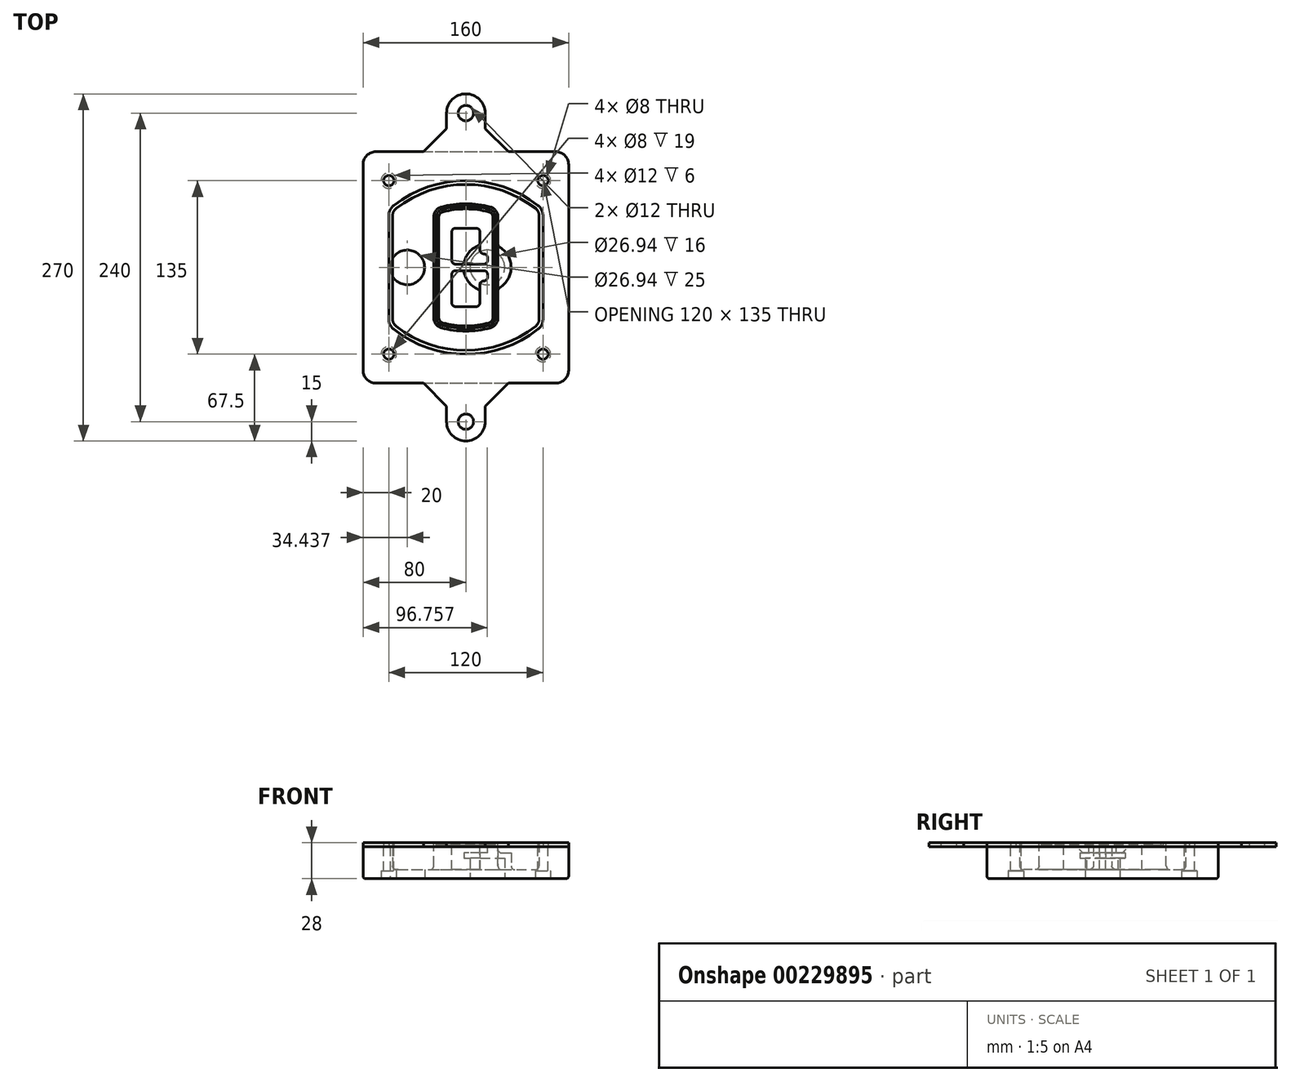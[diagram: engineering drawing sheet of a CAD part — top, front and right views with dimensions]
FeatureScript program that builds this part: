
annotation { "Feature Type Name" : "Feature", "Feature Type Description" : "" }
export const myFeature = defineFeature(function(context is Context, id is Id, definition is map)
    precondition{}
    {
        {
            var Q0;
            Q0=qCreatedBy(makeId("Top.planeOp"),FACE);
            var sketch = newSketch(context, id + "F0", { "sketchPlane" : qUnion([Q0])});
            skPoint(sketch, "E0.rect.middle", {"position": v(0, 0) * mm});
            skLineSegment(sketch, "E1.bottom", {"start": v(-70, -90) * mm, "end": v(70, -90) * mm});
            skLineSegment(sketch, "E1.top", {"start": v(-70, 90) * mm, "end": v(70, 90) * mm});
            skLineSegment(sketch, "E1.left", {"start": v(-80, -80) * mm, "end": v(-80, 80) * mm});
            skLineSegment(sketch, "E1.right", {"start": v(80, -80) * mm, "end": v(80, 80) * mm});
            skLineSegment(sketch, "E2", {"start": v(-80, 90) * mm, "end": v(80, -90) * mm, "construction": true});
            skLineSegment(sketch, "E3", {"start": v(80, 90) * mm, "end": v(-80, -90) * mm, "construction": true});
            skCircle(sketch, "E4", {"center": v(-60, 67.5) * mm, "radius": 4 * mm});
            skCircle(sketch, "E5", {"center": v(60, 67.5) * mm, "radius": 4 * mm});
            skCircle(sketch, "E6", {"center": v(60, -67.5) * mm, "radius": 4 * mm});
            skCircle(sketch, "E7", {"center": v(-60, -67.5) * mm, "radius": 4 * mm});
            skLineSegment(sketch, "E8", {"start": v(-60, 67.5) * mm, "end": v(60, 67.5) * mm, "construction": true});
            skLineSegment(sketch, "E9", {"start": v(60, 67.5) * mm, "end": v(60, -67.5) * mm, "construction": true});
            skLineSegment(sketch, "E10", {"start": v(60, -67.5) * mm, "end": v(-60, -67.5) * mm, "construction": true});
            skLineSegment(sketch, "E11", {"start": v(-60, -67.5) * mm, "end": v(-60, 67.5) * mm, "construction": true});
            skLineSegment(sketch, "E12", {"start": v(-60, 40.3) * mm, "end": v(-60, -40.3) * mm});
            skLineSegment(sketch, "E13", {"start": v(60, 40.3) * mm, "end": v(60, -40.3) * mm});
            skArc(sketch, "E14", {"start": v(56.15, 48.18) * mm, "mid": v(0, 67.5) * mm, "end": v(-56.15, 48.18) * mm});
            skArc(sketch, "E15", {"start": v(-56.15, -48.18) * mm, "mid": v(0, -67.5) * mm, "end": v(56.15, -48.18) * mm});
            skLineSegment(sketch, "E16", {"start": v(-60, 0) * mm, "end": v(60, 0) * mm, "construction": true});
            skPoint(sketch, "E17.visualSharp", {"position": v(-60, -45) * mm});
            skArc(sketch, "E17.filletArc", {"start": v(-60, -40.3) * mm, "mid": v(-58.99, -44.68) * mm, "end": v(-56.15, -48.18) * mm});
            skPoint(sketch, "E18.visualSharp", {"position": v(-60, 45) * mm});
            skArc(sketch, "E18.filletArc", {"start": v(-56.15, 48.18) * mm, "mid": v(-58.99, 44.68) * mm, "end": v(-60, 40.3) * mm});
            skPoint(sketch, "E19.visualSharp", {"position": v(60, 45) * mm});
            skArc(sketch, "E19.filletArc", {"start": v(60, 40.3) * mm, "mid": v(58.99, 44.68) * mm, "end": v(56.15, 48.18) * mm});
            skPoint(sketch, "E20.visualSharp", {"position": v(60, -45) * mm});
            skArc(sketch, "E20.filletArc", {"start": v(56.15, -48.18) * mm, "mid": v(58.99, -44.68) * mm, "end": v(60, -40.3) * mm});
            skPoint(sketch, "E21.visualSharp", {"position": v(-80, 90) * mm});
            skArc(sketch, "E21.filletArc", {"start": v(-70, 90) * mm, "mid": v(-77.07, 87.07) * mm, "end": v(-80, 80) * mm});
            skPoint(sketch, "E22.visualSharp", {"position": v(80, 90) * mm});
            skArc(sketch, "E22.filletArc", {"start": v(80, 80) * mm, "mid": v(77.07, 87.07) * mm, "end": v(70, 90) * mm});
            skPoint(sketch, "E23.visualSharp", {"position": v(80, -90) * mm});
            skArc(sketch, "E23.filletArc", {"start": v(70, -90) * mm, "mid": v(77.07, -87.07) * mm, "end": v(80, -80) * mm});
            skPoint(sketch, "E24.visualSharp", {"position": v(-80, -90) * mm});
            skArc(sketch, "E24.filletArc", {"start": v(-80, -80) * mm, "mid": v(-77.07, -87.07) * mm, "end": v(-70, -90) * mm});
            skArc(sketch, "E25.0", {"start": v(57, 40.3) * mm, "mid": v(56.3, 43.36) * mm, "end": v(54.3, 45.81) * mm});
            skLineSegment(sketch, "E25.1", {"start": v(57, 40.3) * mm, "end": v(57, -40.3) * mm});
            skArc(sketch, "E25.2", {"start": v(54.3, -45.81) * mm, "mid": v(56.3, -43.36) * mm, "end": v(57, -40.3) * mm});
            skArc(sketch, "E25.3", {"start": v(-54.3, -45.81) * mm, "mid": v(0, -64.5) * mm, "end": v(54.3, -45.81) * mm});
            skArc(sketch, "E25.4", {"start": v(-57, -40.3) * mm, "mid": v(-56.3, -43.36) * mm, "end": v(-54.3, -45.81) * mm});
            skArc(sketch, "E25.5", {"start": v(54.3, 45.81) * mm, "mid": v(0, 64.5) * mm, "end": v(-54.3, 45.81) * mm});
            skLineSegment(sketch, "E25.6", {"start": v(-57, 40.3) * mm, "end": v(-57, -40.3) * mm});
            skArc(sketch, "E25.7", {"start": v(-54.3, 45.81) * mm, "mid": v(-56.3, 43.36) * mm, "end": v(-57, 40.3) * mm});
            skArc(sketch, "E26.0", {"start": v(-58.62, 51.33) * mm, "mid": v(-62.58, 46.43) * mm, "end": v(-64, 40.3) * mm});
            skArc(sketch, "E26.1", {"start": v(58.62, 51.33) * mm, "mid": v(0, 71.5) * mm, "end": v(-58.62, 51.33) * mm});
            skArc(sketch, "E26.2", {"start": v(64, 40.3) * mm, "mid": v(62.58, 46.43) * mm, "end": v(58.62, 51.33) * mm});
            skLineSegment(sketch, "E26.3", {"start": v(64, 40.3) * mm, "end": v(64, -40.3) * mm});
            skArc(sketch, "E26.4", {"start": v(58.62, -51.33) * mm, "mid": v(62.58, -46.43) * mm, "end": v(64, -40.3) * mm});
            skLineSegment(sketch, "E26.5", {"start": v(-64, 40.3) * mm, "end": v(-64, -40.3) * mm});
            skArc(sketch, "E26.6", {"start": v(-58.62, -51.33) * mm, "mid": v(0, -71.5) * mm, "end": v(58.62, -51.33) * mm});
            skArc(sketch, "E26.7", {"start": v(-64, -40.3) * mm, "mid": v(-62.58, -46.43) * mm, "end": v(-58.62, -51.33) * mm});
            skSolve(sketch);
        }
        {
            var Q0;
            Q0=makeQuery(id+"F0.imprint","IMPRINT",FACE,{"disambiguationData":[TD([[makeQuery(id+"F0.imprint","IMPRINT",EDGE,{"derivedFrom":sQuery(id+"F0.wireOp",EDGE,"E1.bottom")}),1.0]])]});
            var Q1;
            Q1=makeQuery(id+"F0.imprint","IMPRINT",FACE,{"disambiguationData":[TD([[makeQuery(id+"F0.imprint","IMPRINT",EDGE,{"derivedFrom":sQuery(id+"F0.wireOp",EDGE,"E12")}),1.0]])]});
            var Q2;
            Q2=makeQuery(id+"F0.imprint","IMPRINT",FACE,{"disambiguationData":[TD([[makeQuery(id+"F0.imprint","IMPRINT",EDGE,{"derivedFrom":sQuery(id+"F0.wireOp",EDGE,"E25.0")}),1.0]])]});
            var Q3;
            Q3=makeQuery(id+"F0.imprint","IMPRINT",FACE,{"disambiguationData":[TD([[makeQuery(id+"F0.imprint","IMPRINT",EDGE,{"derivedFrom":sQuery(id+"F0.wireOp",EDGE,"E12")}),-1.0]])]});
            extrude(context, id + "F1", {"entities" : qUnion([Q0, Q1, Q2, Q3]), "oppositeDirection" : true, "depth" : 25 * mm});
        }
        {
            var Q0;
            Q0=makeQuery(id+"F0.imprint","IMPRINT",FACE,{"disambiguationData":[TD([[makeQuery(id+"F0.imprint","IMPRINT",EDGE,{"derivedFrom":sQuery(id+"F0.wireOp",EDGE,"E12")}),1.0]])]});
            extrude(context, id + "F2", {"entities" : qUnion([Q0]), "operationType" : NewBodyOperationType.ADD, "depth" : 3 * mm});
        }
        {
            var Q0;
            Q0=makeQuery(id+"F0.imprint","IMPRINT",FACE,{"disambiguationData":[TD([[makeQuery(id+"F0.imprint","IMPRINT",EDGE,{"derivedFrom":sQuery(id+"F0.wireOp",EDGE,"E25.0")}),1.0]])]});
            extrude(context, id + "F3", {"entities" : qUnion([Q0]), "operationType" : NewBodyOperationType.REMOVE, "oppositeDirection" : true, "depth" : 18 * mm});
        }
        {
            var Q0;
            Q0=makeQuery(id+"F2.opExtrude","CAP_FACE",FACE,{"disambiguationData":[OSD([sQuery(id+"F0.wireOp",EDGE,"E12"),sQuery(id+"F0.wireOp",EDGE,"E13"),sQuery(id+"F0.wireOp",EDGE,"E14"),sQuery(id+"F0.wireOp",EDGE,"E15"),sQuery(id+"F0.wireOp",EDGE,"E17.filletArc"),sQuery(id+"F0.wireOp",EDGE,"E18.filletArc"),sQuery(id+"F0.wireOp",EDGE,"E19.filletArc"),sQuery(id+"F0.wireOp",EDGE,"E20.filletArc"),sQuery(id+"F0.wireOp",EDGE,"E25.0"),sQuery(id+"F0.wireOp",EDGE,"E25.1"),sQuery(id+"F0.wireOp",EDGE,"E25.2"),sQuery(id+"F0.wireOp",EDGE,"E25.3"),sQuery(id+"F0.wireOp",EDGE,"E25.4"),sQuery(id+"F0.wireOp",EDGE,"E25.5"),sQuery(id+"F0.wireOp",EDGE,"E25.6"),sQuery(id+"F0.wireOp",EDGE,"E25.7")])],"isStart":false});
            var sketch = newSketch(context, id + "F4", { "sketchPlane" : qUnion([Q0])});
            skArc(sketch, "E27.0", {"start": v(-19.08, -46.97) * mm, "mid": v(0, -49.5) * mm, "end": v(19.08, -46.97) * mm});
            skArc(sketch, "E28.0", {"start": v(19.08, 46.97) * mm, "mid": v(0, 49.5) * mm, "end": v(-19.08, 46.97) * mm});
            skLineSegment(sketch, "E29", {"start": v(-25, 39.25) * mm, "end": v(-25, -39.25) * mm});
            skLineSegment(sketch, "E30", {"start": v(25, 39.25) * mm, "end": v(25, -39.25) * mm});
            skLineSegment(sketch, "E31", {"start": v(-25, 45.1) * mm, "end": v(25, 45.1) * mm, "construction": true});
            skLineSegment(sketch, "E32", {"start": v(-25, -45.1) * mm, "end": v(25, -45.1) * mm, "construction": true});
            skPoint(sketch, "E33.visualSharp", {"position": v(-25, 45.1) * mm});
            skArc(sketch, "E33.filletArc", {"start": v(-19.08, 46.97) * mm, "mid": v(-23.35, 44.11) * mm, "end": v(-25, 39.25) * mm});
            skPoint(sketch, "E34.visualSharp", {"position": v(25, 45.1) * mm});
            skArc(sketch, "E34.filletArc", {"start": v(25, 39.25) * mm, "mid": v(23.35, 44.11) * mm, "end": v(19.08, 46.97) * mm});
            skPoint(sketch, "E35.visualSharp", {"position": v(25, -45.1) * mm});
            skArc(sketch, "E35.filletArc", {"start": v(19.08, -46.97) * mm, "mid": v(23.35, -44.11) * mm, "end": v(25, -39.25) * mm});
            skPoint(sketch, "E36.visualSharp", {"position": v(-25, -45.1) * mm});
            skArc(sketch, "E36.filletArc", {"start": v(-25, -39.25) * mm, "mid": v(-23.35, -44.11) * mm, "end": v(-19.08, -46.97) * mm});
            skArc(sketch, "E37.0", {"start": v(54.3, 45.81) * mm, "mid": v(0, 64.5) * mm, "end": v(-54.3, 45.81) * mm});
            skArc(sketch, "E37.1", {"start": v(-54.3, 45.81) * mm, "mid": v(-56.3, 43.36) * mm, "end": v(-57, 40.3) * mm});
            skLineSegment(sketch, "E37.2", {"start": v(-57, 40.3) * mm, "end": v(-57, -40.3) * mm});
            skArc(sketch, "E37.3", {"start": v(-57, -40.3) * mm, "mid": v(-56.3, -43.36) * mm, "end": v(-54.3, -45.81) * mm});
            skArc(sketch, "E37.4", {"start": v(-54.3, -45.81) * mm, "mid": v(0, -64.5) * mm, "end": v(54.3, -45.81) * mm});
            skArc(sketch, "E37.5", {"start": v(54.3, -45.81) * mm, "mid": v(56.3, -43.36) * mm, "end": v(57, -40.3) * mm});
            skLineSegment(sketch, "E37.6", {"start": v(57, 40.3) * mm, "end": v(57, -40.3) * mm});
            skArc(sketch, "E37.7", {"start": v(57, 40.3) * mm, "mid": v(56.3, 43.36) * mm, "end": v(54.3, 45.81) * mm});
            skLineSegment(sketch, "E38.0", {"start": v(23, 39.25) * mm, "end": v(23, -39.25) * mm});
            skArc(sketch, "E38.1", {"start": v(18.56, -45.04) * mm, "mid": v(21.76, -42.9) * mm, "end": v(23, -39.25) * mm});
            skArc(sketch, "E38.2", {"start": v(-18.56, -45.04) * mm, "mid": v(0, -47.5) * mm, "end": v(18.56, -45.04) * mm});
            skArc(sketch, "E38.3", {"start": v(-23, -39.25) * mm, "mid": v(-21.76, -42.9) * mm, "end": v(-18.56, -45.04) * mm});
            skLineSegment(sketch, "E38.4", {"start": v(-23, 39.25) * mm, "end": v(-23, -39.25) * mm});
            skArc(sketch, "E38.5", {"start": v(23, 39.25) * mm, "mid": v(21.76, 42.9) * mm, "end": v(18.56, 45.04) * mm});
            skArc(sketch, "E38.6", {"start": v(-18.56, 45.04) * mm, "mid": v(-21.76, 42.9) * mm, "end": v(-23, 39.25) * mm});
            skArc(sketch, "E38.7", {"start": v(18.56, 45.04) * mm, "mid": v(0, 47.5) * mm, "end": v(-18.56, 45.04) * mm});
            skArc(sketch, "E39.0", {"start": v(21, 39.25) * mm, "mid": v(20.18, 41.68) * mm, "end": v(18.04, 43.1) * mm});
            skLineSegment(sketch, "E39.1", {"start": v(21, 39.25) * mm, "end": v(21, -39.25) * mm});
            skArc(sketch, "E39.2", {"start": v(18.04, -43.1) * mm, "mid": v(20.18, -41.68) * mm, "end": v(21, -39.25) * mm});
            skArc(sketch, "E39.3", {"start": v(-18.04, -43.1) * mm, "mid": v(0, -45.5) * mm, "end": v(18.04, -43.1) * mm});
            skArc(sketch, "E39.4", {"start": v(-21, -39.25) * mm, "mid": v(-20.18, -41.68) * mm, "end": v(-18.04, -43.1) * mm});
            skArc(sketch, "E39.5", {"start": v(18.04, 43.1) * mm, "mid": v(0, 45.5) * mm, "end": v(-18.04, 43.1) * mm});
            skLineSegment(sketch, "E39.6", {"start": v(-21, 39.25) * mm, "end": v(-21, -39.25) * mm});
            skArc(sketch, "E39.7", {"start": v(-18.04, 43.1) * mm, "mid": v(-20.18, 41.68) * mm, "end": v(-21, 39.25) * mm});
            skLineSegment(sketch, "E40", {"start": v(-25, 0) * mm, "end": v(25, 0) * mm, "construction": true});
            skLineSegment(sketch, "E41", {"start": v(-11, 5.5) * mm, "end": v(-11, 27.5) * mm});
            skLineSegment(sketch, "E42", {"start": v(-8, 30.5) * mm, "end": v(8, 30.5) * mm});
            skLineSegment(sketch, "E43", {"start": v(11, 27.5) * mm, "end": v(11, 13.5) * mm});
            skLineSegment(sketch, "E44", {"start": v(14, 10.5) * mm, "end": v(14, 10.5) * mm});
            skLineSegment(sketch, "E45", {"start": v(17, 7.5) * mm, "end": v(17, 5.5) * mm});
            skLineSegment(sketch, "E46", {"start": v(14, 2.5) * mm, "end": v(-8, 2.5) * mm});
            skPoint(sketch, "E47.visualSharp", {"position": v(-11, 30.5) * mm});
            skArc(sketch, "E47.filletArc", {"start": v(-8, 30.5) * mm, "mid": v(-10.12, 29.62) * mm, "end": v(-11, 27.5) * mm});
            skPoint(sketch, "E48.visualSharp", {"position": v(11, 30.5) * mm});
            skArc(sketch, "E48.filletArc", {"start": v(11, 27.5) * mm, "mid": v(10.12, 29.62) * mm, "end": v(8, 30.5) * mm});
            skPoint(sketch, "E49.visualSharp", {"position": v(11, 10.5) * mm});
            skArc(sketch, "E49.filletArc", {"start": v(11, 13.5) * mm, "mid": v(11.88, 11.38) * mm, "end": v(14, 10.5) * mm});
            skPoint(sketch, "E50.visualSharp", {"position": v(17, 10.5) * mm});
            skArc(sketch, "E50.filletArc", {"start": v(17, 7.5) * mm, "mid": v(16.12, 9.62) * mm, "end": v(14, 10.5) * mm});
            skPoint(sketch, "E51.visualSharp", {"position": v(17, 2.5) * mm});
            skArc(sketch, "E51.filletArc", {"start": v(14, 2.5) * mm, "mid": v(16.12, 3.38) * mm, "end": v(17, 5.5) * mm});
            skPoint(sketch, "E52.visualSharp", {"position": v(-11, 2.5) * mm});
            skArc(sketch, "E52.filletArc", {"start": v(-11, 5.5) * mm, "mid": v(-10.12, 3.38) * mm, "end": v(-8, 2.5) * mm});
            skLineSegment(sketch, "E53.0.MirrorCS", {"start": v(14, -2.5) * mm, "end": v(-8, -2.5) * mm});
            skArc(sketch, "E54.0.MirrorCS", {"start": v(-11, -5.5) * mm, "mid": v(-10.12, -3.38) * mm, "end": v(-8, -2.5) * mm});
            skLineSegment(sketch, "E55.0.MirrorCS", {"start": v(-11, -5.5) * mm, "end": v(-11, -27.5) * mm});
            skArc(sketch, "E56.0.MirrorCS", {"start": v(-8, -30.5) * mm, "mid": v(-10.12, -29.62) * mm, "end": v(-11, -27.5) * mm});
            skLineSegment(sketch, "E57.0.MirrorCS", {"start": v(-8, -30.5) * mm, "end": v(8, -30.5) * mm});
            skArc(sketch, "E58.0.MirrorCS", {"start": v(11, -27.5) * mm, "mid": v(10.12, -29.62) * mm, "end": v(8, -30.5) * mm});
            skLineSegment(sketch, "E59.0.MirrorCS", {"start": v(11, -27.5) * mm, "end": v(11, -13.5) * mm});
            skArc(sketch, "E60.0.MirrorCS", {"start": v(11, -13.5) * mm, "mid": v(11.88, -11.38) * mm, "end": v(14, -10.5) * mm});
            skArc(sketch, "E61.0.MirrorCS", {"start": v(17, -7.5) * mm, "mid": v(16.12, -9.62) * mm, "end": v(14, -10.5) * mm});
            skLineSegment(sketch, "E62.0.MirrorCS", {"start": v(17, -7.5) * mm, "end": v(17, -5.5) * mm});
            skArc(sketch, "E63.0.MirrorCS", {"start": v(14, -2.5) * mm, "mid": v(16.12, -3.38) * mm, "end": v(17, -5.5) * mm});
            skSolve(sketch);
        }
        {
            var Q0;
            Q0=makeQuery(id+"F4.imprint","IMPRINT",FACE,{"disambiguationData":[TD([[makeQuery(id+"F4.imprint","IMPRINT",EDGE,{"derivedFrom":sQuery(id+"F4.wireOp",EDGE,"E27.0")}),1.0]])]});
            var Q1;
            Q1=makeQuery(id+"F4.imprint","IMPRINT",FACE,{"disambiguationData":[TD([[makeQuery(id+"F4.imprint","IMPRINT",EDGE,{"derivedFrom":sQuery(id+"F4.wireOp",EDGE,"E38.0")}),-1.0]])]});
            var Q2;
            Q2=makeQuery(id+"F4.imprint","IMPRINT",FACE,{"disambiguationData":[TD([[makeQuery(id+"F4.imprint","IMPRINT",EDGE,{"derivedFrom":sQuery(id+"F4.wireOp",EDGE,"E39.0")}),1.0]])]});
            extrude(context, id + "F5", {"entities" : qUnion([Q0, Q1, Q2]), "operationType" : NewBodyOperationType.ADD, "endBound" : BoundingType.UP_TO_NEXT, "oppositeDirection" : true, "depth" : 25 * mm});
        }
        {
            var Q0;
            Q0=makeQuery(id+"F4.imprint","IMPRINT",FACE,{"disambiguationData":[TD([[makeQuery(id+"F4.imprint","IMPRINT",EDGE,{"derivedFrom":sQuery(id+"F4.wireOp",EDGE,"E38.0")}),-1.0]])]});
            extrude(context, id + "F6", {"entities" : qUnion([Q0]), "operationType" : NewBodyOperationType.REMOVE, "oppositeDirection" : true, "depth" : 2 * mm});
        }
        {
            var Q0;
            Q0=makeQuery(id+"F1.opExtrude","CAP_FACE",FACE,{"disambiguationData":[OSD([sQuery(id+"F0.wireOp",EDGE,"E1.bottom"),sQuery(id+"F0.wireOp",EDGE,"E1.top"),sQuery(id+"F0.wireOp",EDGE,"E1.left"),sQuery(id+"F0.wireOp",EDGE,"E1.right"),sQuery(id+"F0.wireOp",EDGE,"E4"),sQuery(id+"F0.wireOp",EDGE,"E5"),sQuery(id+"F0.wireOp",EDGE,"E6"),sQuery(id+"F0.wireOp",EDGE,"E7"),sQuery(id+"F0.wireOp",EDGE,"E21.filletArc"),sQuery(id+"F0.wireOp",EDGE,"E22.filletArc"),sQuery(id+"F0.wireOp",EDGE,"E23.filletArc"),sQuery(id+"F0.wireOp",EDGE,"E24.filletArc")])],"isStart":false});
            var sketch = newSketch(context, id + "F7", { "sketchPlane" : qUnion([Q0])});
            skCircle(sketch, "E64", {"center": v(16.76, 0) * mm, "radius": 13.47 * mm});
            skCircle(sketch, "E65", {"center": v(-45.56, 0) * mm, "radius": 13.47 * mm});
            skLineSegment(sketch, "E66", {"start": v(80, 0) * mm, "end": v(-80, 0) * mm});
            skCircle(sketch, "E67", {"center": v(16.76, 0) * mm, "radius": 18.47 * mm});
            skCircle(sketch, "E68", {"center": v(60, -67.5) * mm, "radius": 6 * mm});
            skCircle(sketch, "E69", {"center": v(-60, -67.5) * mm, "radius": 6 * mm});
            skCircle(sketch, "E70", {"center": v(-60, 67.5) * mm, "radius": 6 * mm});
            skCircle(sketch, "E71", {"center": v(60, 67.5) * mm, "radius": 6 * mm});
            skSolve(sketch);
        }
        {
            var Q0;
            {var subQ1=sQuery(id+"F7.wireOp",EDGE,"E66");var subQ4=sQuery(id+"F7.wireOp",EDGE,"E64");var subQ6=makeQuery(id+"F7.imprint","INTERSECT",VERTEX,{"disambiguationData":[OD(0.0)],"derivedFrom":[subQ4,subQ1]});Q0=makeQuery(id+"F7.imprint","IMPRINT",FACE,{"disambiguationData":[TD([[makeQuery(id+"F7.imprint","IMPRINT",EDGE,{"disambiguationData":[TD([[subQ6,-1.0]])],"derivedFrom":subQ4}),-1.0]])]});}
            var Q1;
            {var subQ0=sQuery(id+"F7.wireOp",EDGE,"E66");var subQ1=sQuery(id+"F7.wireOp",EDGE,"E64");var subQ3=makeQuery(id+"F7.imprint","INTERSECT",VERTEX,{"disambiguationData":[OD(0.0)],"derivedFrom":[subQ1,subQ0]});Q1=makeQuery(id+"F7.imprint","IMPRINT",FACE,{"disambiguationData":[TD([[makeQuery(id+"F7.imprint","IMPRINT",EDGE,{"disambiguationData":[TD([[subQ3,-1.0]])],"derivedFrom":subQ1}),1.0]])]});}
            var Q2;
            {var subQ0=sQuery(id+"F7.wireOp",EDGE,"E66");var subQ1=sQuery(id+"F7.wireOp",EDGE,"E64");var subQ3=makeQuery(id+"F7.imprint","INTERSECT",VERTEX,{"disambiguationData":[OD(0.0)],"derivedFrom":[subQ1,subQ0]});Q2=makeQuery(id+"F7.imprint","IMPRINT",FACE,{"disambiguationData":[TD([[makeQuery(id+"F7.imprint","IMPRINT",EDGE,{"disambiguationData":[TD([[subQ3,1.0]])],"derivedFrom":subQ1}),1.0]])]});}
            var Q3;
            {var subQ1=sQuery(id+"F7.wireOp",EDGE,"E66");var subQ4=sQuery(id+"F7.wireOp",EDGE,"E64");var subQ6=makeQuery(id+"F7.imprint","INTERSECT",VERTEX,{"disambiguationData":[OD(0.0)],"derivedFrom":[subQ4,subQ1]});Q3=makeQuery(id+"F7.imprint","IMPRINT",FACE,{"disambiguationData":[TD([[makeQuery(id+"F7.imprint","IMPRINT",EDGE,{"disambiguationData":[TD([[subQ6,1.0]])],"derivedFrom":subQ4}),-1.0]])]});}
            extrude(context, id + "F8", {"entities" : qUnion([Q0, Q1, Q2, Q3]), "operationType" : NewBodyOperationType.ADD, "oppositeDirection" : true, "depth" : 20 * mm});
        }
        {
            var Q0;
            {var subQ0=sQuery(id+"F7.wireOp",EDGE,"E66");var subQ1=sQuery(id+"F7.wireOp",EDGE,"E64");var subQ3=makeQuery(id+"F7.imprint","INTERSECT",VERTEX,{"disambiguationData":[OD(0.0)],"derivedFrom":[subQ1,subQ0]});Q0=makeQuery(id+"F7.imprint","IMPRINT",FACE,{"disambiguationData":[TD([[makeQuery(id+"F7.imprint","IMPRINT",EDGE,{"disambiguationData":[TD([[subQ3,-1.0]])],"derivedFrom":subQ1}),1.0]])]});}
            var Q1;
            {var subQ0=sQuery(id+"F7.wireOp",EDGE,"E66");var subQ1=sQuery(id+"F7.wireOp",EDGE,"E64");var subQ3=makeQuery(id+"F7.imprint","INTERSECT",VERTEX,{"disambiguationData":[OD(0.0)],"derivedFrom":[subQ1,subQ0]});Q1=makeQuery(id+"F7.imprint","IMPRINT",FACE,{"disambiguationData":[TD([[makeQuery(id+"F7.imprint","IMPRINT",EDGE,{"disambiguationData":[TD([[subQ3,1.0]])],"derivedFrom":subQ1}),1.0]])]});}
            extrude(context, id + "F9", {"entities" : qUnion([Q0, Q1]), "operationType" : NewBodyOperationType.REMOVE, "oppositeDirection" : true, "depth" : 16 * mm});
        }
        {
            var Q0;
            {var subQ0=sQuery(id+"F7.wireOp",EDGE,"E66");var subQ1=sQuery(id+"F7.wireOp",EDGE,"E65");var subQ3=makeQuery(id+"F7.imprint","INTERSECT",VERTEX,{"disambiguationData":[OD(0.0)],"derivedFrom":[subQ1,subQ0]});Q0=makeQuery(id+"F7.imprint","IMPRINT",FACE,{"disambiguationData":[TD([[makeQuery(id+"F7.imprint","IMPRINT",EDGE,{"disambiguationData":[TD([[subQ3,-1.0]])],"derivedFrom":subQ1}),1.0]])]});}
            var Q1;
            {var subQ0=sQuery(id+"F7.wireOp",EDGE,"E66");var subQ1=sQuery(id+"F7.wireOp",EDGE,"E65");var subQ3=makeQuery(id+"F7.imprint","INTERSECT",VERTEX,{"disambiguationData":[OD(0.0)],"derivedFrom":[subQ1,subQ0]});Q1=makeQuery(id+"F7.imprint","IMPRINT",FACE,{"disambiguationData":[TD([[makeQuery(id+"F7.imprint","IMPRINT",EDGE,{"disambiguationData":[TD([[subQ3,1.0]])],"derivedFrom":subQ1}),1.0]])]});}
            extrude(context, id + "F10", {"entities" : qUnion([Q0, Q1]), "operationType" : NewBodyOperationType.REMOVE, "oppositeDirection" : true, "depth" : 25 * mm});
        }
        {
            var Q0;
            Q0=makeQuery(id+"F7.imprint","IMPRINT",FACE,{"disambiguationData":[TD([[makeQuery(id+"F7.imprint","IMPRINT",EDGE,{"derivedFrom":sQuery(id+"F7.wireOp",EDGE,"E68")}),1.0]])]});
            var Q1;
            Q1=makeQuery(id+"F7.imprint","IMPRINT",FACE,{"disambiguationData":[TD([[makeQuery(id+"F7.imprint","IMPRINT",EDGE,{"derivedFrom":makeQuery(id+"F1.opExtrude","CAP_EDGE",EDGE,{"disambiguationData":[OSD([sQuery(id+"F0.wireOp",EDGE,"E5")])],"isStart":false})}),-1.0]])]});
            var Q2;
            Q2=makeQuery(id+"F7.imprint","IMPRINT",FACE,{"disambiguationData":[TD([[makeQuery(id+"F7.imprint","IMPRINT",EDGE,{"derivedFrom":sQuery(id+"F7.wireOp",EDGE,"E69")}),1.0]])]});
            var Q3;
            Q3=makeQuery(id+"F7.imprint","IMPRINT",FACE,{"disambiguationData":[TD([[makeQuery(id+"F7.imprint","IMPRINT",EDGE,{"derivedFrom":makeQuery(id+"F1.opExtrude","CAP_EDGE",EDGE,{"disambiguationData":[OSD([sQuery(id+"F0.wireOp",EDGE,"E4")])],"isStart":false})}),-1.0]])]});
            var Q4;
            Q4=makeQuery(id+"F7.imprint","IMPRINT",FACE,{"disambiguationData":[TD([[makeQuery(id+"F7.imprint","IMPRINT",EDGE,{"derivedFrom":sQuery(id+"F7.wireOp",EDGE,"E70")}),1.0]])]});
            var Q5;
            Q5=makeQuery(id+"F7.imprint","IMPRINT",FACE,{"disambiguationData":[TD([[makeQuery(id+"F7.imprint","IMPRINT",EDGE,{"derivedFrom":makeQuery(id+"F1.opExtrude","CAP_EDGE",EDGE,{"disambiguationData":[OSD([sQuery(id+"F0.wireOp",EDGE,"E7")])],"isStart":false})}),-1.0]])]});
            var Q6;
            Q6=makeQuery(id+"F7.imprint","IMPRINT",FACE,{"disambiguationData":[TD([[makeQuery(id+"F7.imprint","IMPRINT",EDGE,{"derivedFrom":sQuery(id+"F7.wireOp",EDGE,"E71")}),1.0]])]});
            var Q7;
            Q7=makeQuery(id+"F7.imprint","IMPRINT",FACE,{"disambiguationData":[TD([[makeQuery(id+"F7.imprint","IMPRINT",EDGE,{"derivedFrom":makeQuery(id+"F1.opExtrude","CAP_EDGE",EDGE,{"disambiguationData":[OSD([sQuery(id+"F0.wireOp",EDGE,"E6")])],"isStart":false})}),-1.0]])]});
            extrude(context, id + "F11", {"entities" : qUnion([Q0, Q1, Q2, Q3, Q4, Q5, Q6, Q7]), "operationType" : NewBodyOperationType.REMOVE, "oppositeDirection" : true, "depth" : 6 * mm});
        }
        {
            var Q0;
            Q0=makeQuery(id+"F9.boolean.opBoolean","COPY",FACE,{"derivedFrom":makeQuery(id+"F9.opExtrude","CAP_FACE",FACE,{"disambiguationData":[OSD([sQuery(id+"F7.wireOp",EDGE,"E64")])],"isStart":false})});
            var sketch = newSketch(context, id + "F12", { "sketchPlane" : qUnion([Q0])});
            skArc(sketch, "E72.0", {"start": v(11, 17.55) * mm, "mid": v(2.57, 11.82) * mm, "end": v(-1.54, 2.5) * mm});
            skArc(sketch, "E72.1", {"start": v(-1.54, -2.5) * mm, "mid": v(2.57, -11.82) * mm, "end": v(11, -17.55) * mm});
            skLineSegment(sketch, "E73", {"start": v(-1.54, -2.5) * mm, "end": v(14, -2.5) * mm});
            skLineSegment(sketch, "E74.0", {"start": v(14, 2.5) * mm, "end": v(-1.54, 2.5) * mm});
            skArc(sketch, "E74.1", {"start": v(14, 2.5) * mm, "mid": v(16.12, 3.38) * mm, "end": v(17, 5.5) * mm});
            skLineSegment(sketch, "E74.2", {"start": v(17, 7.5) * mm, "end": v(17, 5.5) * mm});
            skArc(sketch, "E74.3", {"start": v(17, 7.5) * mm, "mid": v(16.12, 9.62) * mm, "end": v(14, 10.5) * mm});
            skArc(sketch, "E74.4", {"start": v(11, 13.5) * mm, "mid": v(11.88, 11.38) * mm, "end": v(14, 10.5) * mm});
            skLineSegment(sketch, "E74.5", {"start": v(11, 17.55) * mm, "end": v(11, 13.5) * mm});
            skLineSegment(sketch, "E74.7", {"start": v(14, -2.5) * mm, "end": v(-1.54, -2.5) * mm});
            skArc(sketch, "E74.8", {"start": v(14, -2.5) * mm, "mid": v(16.12, -3.38) * mm, "end": v(17, -5.5) * mm});
            skLineSegment(sketch, "E74.9", {"start": v(17, -7.5) * mm, "end": v(17, -5.5) * mm});
            skArc(sketch, "E74.10", {"start": v(17, -7.5) * mm, "mid": v(16.12, -9.62) * mm, "end": v(14, -10.5) * mm});
            skArc(sketch, "E74.11", {"start": v(11, -13.5) * mm, "mid": v(11.88, -11.38) * mm, "end": v(14, -10.5) * mm});
            skLineSegment(sketch, "E74.12", {"start": v(11, -17.55) * mm, "end": v(11, -13.5) * mm});
            skPoint(sketch, "E75.orphan", {"position": v(11, -27.5) * mm});
            skPoint(sketch, "E76.orphan", {"position": v(-8, -2.5) * mm});
            skPoint(sketch, "E77.orphan", {"position": v(-8, 2.5) * mm});
            skPoint(sketch, "E78.orphan", {"position": v(11, 27.5) * mm});
            skSolve(sketch);
        }
        {
            var Q0;
            {var subQ7=sQuery(id+"F12.wireOp",EDGE,"E72.0");var subQ14=sQuery(id+"F12.wireOp",EDGE,"E72.1");var subQ16=sQuery(id+"F12.wireOp",EDGE,"E74.1");var subQ18=sQuery(id+"F12.wireOp",EDGE,"E74.8");Q0=qUnion([makeQuery(id+"F12.imprint","IMPRINT",FACE,{"disambiguationData":[TD([[makeQuery(id+"F12.imprint","IMPRINT",EDGE,{"derivedFrom":subQ7}),1.0]])]}),makeQuery(id+"F12.imprint","IMPRINT",FACE,{"disambiguationData":[TD([[makeQuery(id+"F12.imprint","IMPRINT",EDGE,{"derivedFrom":subQ14}),1.0]])]}),makeQuery(id+"F12.imprint","IMPRINT",FACE,{"disambiguationData":[TD([[makeQuery(id+"F12.imprint","IMPRINT",EDGE,{"derivedFrom":subQ16}),1.0]])]}),makeQuery(id+"F12.imprint","IMPRINT",FACE,{"disambiguationData":[TD([[makeQuery(id+"F12.imprint","IMPRINT",EDGE,{"derivedFrom":subQ18}),-1.0]])]})]);}
            var Q1;
            Q1=makeQuery(id+"F5.boolean.opBoolean","SPLIT",FACE,{"disambiguationData":[TD([makeQuery(id+"F5.opExtrude","SWEPT_FACE",FACE,{"disambiguationData":[OSD([sQuery(id+"F4.wireOp",EDGE,"E41")])]})])],"derivedFrom":makeQuery(id+"F3.boolean.opBoolean","COPY",FACE,{"derivedFrom":makeQuery(id+"F3.opExtrude","CAP_FACE",FACE,{"disambiguationData":[OSD([sQuery(id+"F0.wireOp",EDGE,"E25.0"),sQuery(id+"F0.wireOp",EDGE,"E25.1"),sQuery(id+"F0.wireOp",EDGE,"E25.2"),sQuery(id+"F0.wireOp",EDGE,"E25.3"),sQuery(id+"F0.wireOp",EDGE,"E25.4"),sQuery(id+"F0.wireOp",EDGE,"E25.5"),sQuery(id+"F0.wireOp",EDGE,"E25.6"),sQuery(id+"F0.wireOp",EDGE,"E25.7")])],"isStart":false})})});
            extrude(context, id + "F13", {"entities" : qUnion([Q0]), "operationType" : NewBodyOperationType.REMOVE, "endBound" : BoundingType.UP_TO_SURFACE, "endBoundEntityFace" : qUnion([Q1]), "depth" : 25 * mm});
        }
        {
            var Q0;
            Q0=makeQuery(id+"F3.boolean.opBoolean","COPY",EDGE,{"derivedFrom":makeQuery(id+"F3.opExtrude","CAP_EDGE",EDGE,{"disambiguationData":[OSD([sQuery(id+"F0.wireOp",EDGE,"E25.6")])],"isStart":false})});
            var Q1;
            Q1=makeQuery(id+"F8.boolean.opBoolean","INTERSECT",EDGE,{"derivedFrom":[makeQuery(id+"F5.opExtrude","SWEPT_FACE",FACE,{"disambiguationData":[OSD([sQuery(id+"F4.wireOp",EDGE,"E30")])]}),makeQuery(id+"F8.opExtrude","CAP_FACE",FACE,{"disambiguationData":[OSD([sQuery(id+"F7.wireOp",EDGE,"E67")])],"isStart":false})]});
            var Q2;
            Q2=makeQuery(id+"F8.boolean.opBoolean","INTERSECT",EDGE,{"disambiguationData":[OD(1.0)],"derivedFrom":[makeQuery(id+"F5.opExtrude","SWEPT_FACE",FACE,{"disambiguationData":[OSD([sQuery(id+"F4.wireOp",EDGE,"E30")])]}),makeQuery(id+"F8.opExtrude","SWEPT_FACE",FACE,{"disambiguationData":[OSD([sQuery(id+"F7.wireOp",EDGE,"E67")])]})]});
            var Q3;
            {var subQ0=sQuery(id+"F4.wireOp",EDGE,"E30");Q3=makeQuery(id+"F8.boolean.opBoolean","SPLIT",EDGE,{"disambiguationData":[TD([makeQuery(id+"F5.opExtrude","SWEPT_FACE",FACE,{"disambiguationData":[OSD([sQuery(id+"F4.wireOp",EDGE,"E35.filletArc")])]})])],"derivedFrom":makeQuery(id+"F5.opExtrude","CAP_EDGE",EDGE,{"disambiguationData":[OSD([subQ0])],"isStart":false})});}
            var Q4;
            {var subQ0=sQuery(id+"F0.wireOp",EDGE,"E25.7");var subQ1=sQuery(id+"F0.wireOp",EDGE,"E25.1");var subQ2=sQuery(id+"F0.wireOp",EDGE,"E25.6");var subQ3=sQuery(id+"F0.wireOp",EDGE,"E25.5");var subQ4=sQuery(id+"F0.wireOp",EDGE,"E25.4");var subQ5=sQuery(id+"F0.wireOp",EDGE,"E25.0");var subQ6=sQuery(id+"F0.wireOp",EDGE,"E25.2");var subQ7=sQuery(id+"F0.wireOp",EDGE,"E25.3");Q4=makeQuery(id+"F8.boolean.opBoolean","INTERSECT",EDGE,{"derivedFrom":[makeQuery(id+"F5.boolean.opBoolean","SPLIT",FACE,{"disambiguationData":[TD([makeQuery(id+"F2.opExtrude","SWEPT_FACE",FACE,{"disambiguationData":[OSD([subQ5])]})])],"derivedFrom":makeQuery(id+"F3.boolean.opBoolean","COPY",FACE,{"derivedFrom":makeQuery(id+"F3.opExtrude","CAP_FACE",FACE,{"disambiguationData":[OSD([subQ5,subQ1,subQ6,subQ7,subQ4,subQ3,subQ2,subQ0])],"isStart":false})})}),makeQuery(id+"F8.opExtrude","SWEPT_FACE",FACE,{"disambiguationData":[OSD([sQuery(id+"F7.wireOp",EDGE,"E67")])]})]});}
            var Q5;
            Q5=makeQuery(id+"F8.boolean.opBoolean","INTERSECT",EDGE,{"disambiguationData":[OD(0.0)],"derivedFrom":[makeQuery(id+"F5.opExtrude","SWEPT_FACE",FACE,{"disambiguationData":[OSD([sQuery(id+"F4.wireOp",EDGE,"E30")])]}),makeQuery(id+"F8.opExtrude","SWEPT_FACE",FACE,{"disambiguationData":[OSD([sQuery(id+"F7.wireOp",EDGE,"E67")])]})]});
            fillet(context, id + "F14", {"entities" : qUnion([Q0, Q1, Q2, Q3, Q4, Q5]), "radius" : 3 * mm, "tangentPropagation" : true, "allowEdgeOverflow" : false});
        }
        {
            var Q0;
            Q0=makeQuery(id+"F1.opExtrude","CAP_EDGE",EDGE,{"disambiguationData":[OSD([sQuery(id+"F0.wireOp",EDGE,"E1.bottom")])],"isStart":false});
            fillet(context, id + "F15", {"entities" : qUnion([Q0]), "radius" : 2 * mm, "tangentPropagation" : true, "allowEdgeOverflow" : false});
        }
        {
            var Q0;
            {var subQ0=sQuery(id+"F0.wireOp",EDGE,"E22.filletArc");var subQ1=sQuery(id+"F0.wireOp",EDGE,"E7");var subQ2=sQuery(id+"F0.wireOp",EDGE,"E6");var subQ3=sQuery(id+"F0.wireOp",EDGE,"E5");var subQ4=sQuery(id+"F0.wireOp",EDGE,"E4");var subQ5=sQuery(id+"F0.wireOp",EDGE,"E1.bottom");var subQ6=sQuery(id+"F0.wireOp",EDGE,"E21.filletArc");var subQ7=sQuery(id+"F0.wireOp",EDGE,"E1.top");var subQ8=sQuery(id+"F0.wireOp",EDGE,"E1.left");var subQ9=sQuery(id+"F0.wireOp",EDGE,"E1.right");var subQ10=sQuery(id+"F0.wireOp",EDGE,"E23.filletArc");var subQ11=sQuery(id+"F0.wireOp",EDGE,"E24.filletArc");Q0=makeQuery(id+"F2.boolean.opBoolean","SPLIT",FACE,{"disambiguationData":[TD([makeQuery(id+"F1.opExtrude","SWEPT_FACE",FACE,{"disambiguationData":[OSD([subQ5])]})])],"derivedFrom":makeQuery(id+"F1.opExtrude","CAP_FACE",FACE,{"disambiguationData":[OSD([subQ5,subQ7,subQ8,subQ9,subQ4,subQ3,subQ2,subQ1,subQ6,subQ0,subQ10,subQ11])],"isStart":true})});}
            var sketch = newSketch(context, id + "F16", { "sketchPlane" : qUnion([Q0])});
            skArc(sketch, "E79.0", {"start": v(-80, -80) * mm, "mid": v(-77.07, -87.07) * mm, "end": v(-70, -90) * mm});
            skLineSegment(sketch, "E79.1", {"start": v(-70, -90) * mm, "end": v(-33, -90) * mm});
            skArc(sketch, "E79.2", {"start": v(70, -90) * mm, "mid": v(77.07, -87.07) * mm, "end": v(80, -80) * mm});
            skLineSegment(sketch, "E79.3", {"start": v(80, -80) * mm, "end": v(80, 80) * mm});
            skArc(sketch, "E79.4", {"start": v(80, 80) * mm, "mid": v(77.07, 87.07) * mm, "end": v(70, 90) * mm});
            skLineSegment(sketch, "E79.5", {"start": v(-70, 90) * mm, "end": v(-33, 90) * mm});
            skArc(sketch, "E79.6", {"start": v(-70, 90) * mm, "mid": v(-77.07, 87.07) * mm, "end": v(-80, 80) * mm});
            skLineSegment(sketch, "E79.7", {"start": v(-80, -80) * mm, "end": v(-80, 80) * mm});
            skCircle(sketch, "E79.8", {"center": v(-60, -67.5) * mm, "radius": 4 * mm});
            skCircle(sketch, "E79.9", {"center": v(-60, 67.5) * mm, "radius": 4 * mm});
            skCircle(sketch, "E79.10", {"center": v(60, 67.5) * mm, "radius": 4 * mm});
            skCircle(sketch, "E79.11", {"center": v(60, -67.5) * mm, "radius": 4 * mm});
            skLineSegment(sketch, "E80", {"start": v(-33, 90) * mm, "end": v(-15, 108) * mm});
            skLineSegment(sketch, "E81", {"start": v(-15, 108) * mm, "end": v(-15, 120) * mm});
            skArc(sketch, "E82", {"start": v(15, 120) * mm, "mid": v(0, 135) * mm, "end": v(-15, 120) * mm});
            skLineSegment(sketch, "E83", {"start": v(15, 120) * mm, "end": v(15, 108) * mm});
            skLineSegment(sketch, "E84", {"start": v(15, 108) * mm, "end": v(33, 90) * mm});
            skLineSegment(sketch, "E85", {"start": v(0, 120) * mm, "end": v(0, 90) * mm, "construction": true});
            skCircle(sketch, "E86", {"center": v(0, 120) * mm, "radius": 6 * mm});
            skLineSegment(sketch, "E87", {"start": v(-80, 0) * mm, "end": v(80, 0) * mm, "construction": true});
            skCircle(sketch, "E88.MirrorC", {"center": v(0, -120) * mm, "radius": 6 * mm});
            skLineSegment(sketch, "E89.MirrorCS", {"start": v(15, -120) * mm, "end": v(15, -108) * mm});
            skLineSegment(sketch, "E90.MirrorCS", {"start": v(-15, -108) * mm, "end": v(-15, -120) * mm});
            skLineSegment(sketch, "E91.MirrorCS", {"start": v(-33, -90) * mm, "end": v(-15, -108) * mm});
            skLineSegment(sketch, "E92.MirrorCS", {"start": v(15, -108) * mm, "end": v(33, -90) * mm});
            skArc(sketch, "E93.MirrorCS", {"start": v(15, -120) * mm, "mid": v(0, -135) * mm, "end": v(-15, -120) * mm});
            skLineSegment(sketch, "E94.MirrorCS", {"start": v(0, -120) * mm, "end": v(0, -90) * mm, "construction": true});
            skLineSegment(sketch, "E95.trimOffspring", {"start": v(33, 90) * mm, "end": v(70, 90) * mm});
            skLineSegment(sketch, "E96.trimOffspring", {"start": v(33, -90) * mm, "end": v(70, -90) * mm});
            skArc(sketch, "E97.0", {"start": v(56.15, 48.18) * mm, "mid": v(0, 67.5) * mm, "end": v(-56.15, 48.18) * mm});
            skArc(sketch, "E98.0", {"start": v(-56.15, 48.18) * mm, "mid": v(-58.99, 44.68) * mm, "end": v(-60, 40.3) * mm});
            skLineSegment(sketch, "E99.0", {"start": v(-60, 40.3) * mm, "end": v(-60, -40.3) * mm});
            skArc(sketch, "E100.0", {"start": v(-56.15, -48.18) * mm, "mid": v(0, -67.5) * mm, "end": v(56.15, -48.18) * mm});
            skArc(sketch, "E101.0", {"start": v(-60, -40.3) * mm, "mid": v(-58.99, -44.68) * mm, "end": v(-56.15, -48.18) * mm});
            skArc(sketch, "E102.0", {"start": v(56.15, -48.18) * mm, "mid": v(58.99, -44.68) * mm, "end": v(60, -40.3) * mm});
            skLineSegment(sketch, "E103.0", {"start": v(60, 40.3) * mm, "end": v(60, -40.3) * mm});
            skArc(sketch, "E104.0", {"start": v(60, 40.3) * mm, "mid": v(58.99, 44.68) * mm, "end": v(56.15, 48.18) * mm});
            skSolve(sketch);
        }
        {
            var Q0;
            Q0 = qSketchRegion(id + "F16", true);
            var Q1;
            Q1=makeQuery(id+"F2.opExtrude","CAP_FACE",FACE,{"disambiguationData":[OSD([sQuery(id+"F0.wireOp",EDGE,"E12"),sQuery(id+"F0.wireOp",EDGE,"E13"),sQuery(id+"F0.wireOp",EDGE,"E14"),sQuery(id+"F0.wireOp",EDGE,"E15"),sQuery(id+"F0.wireOp",EDGE,"E17.filletArc"),sQuery(id+"F0.wireOp",EDGE,"E18.filletArc"),sQuery(id+"F0.wireOp",EDGE,"E19.filletArc"),sQuery(id+"F0.wireOp",EDGE,"E20.filletArc"),sQuery(id+"F0.wireOp",EDGE,"E25.0"),sQuery(id+"F0.wireOp",EDGE,"E25.1"),sQuery(id+"F0.wireOp",EDGE,"E25.2"),sQuery(id+"F0.wireOp",EDGE,"E25.3"),sQuery(id+"F0.wireOp",EDGE,"E25.4"),sQuery(id+"F0.wireOp",EDGE,"E25.5"),sQuery(id+"F0.wireOp",EDGE,"E25.6"),sQuery(id+"F0.wireOp",EDGE,"E25.7")])],"isStart":false});
            extrude(context, id + "F17", {"entities" : qUnion([Q0]), "endBound" : BoundingType.UP_TO_SURFACE, "endBoundEntityFace" : qUnion([Q1]), "depth" : 25 * mm});
        }
    });
